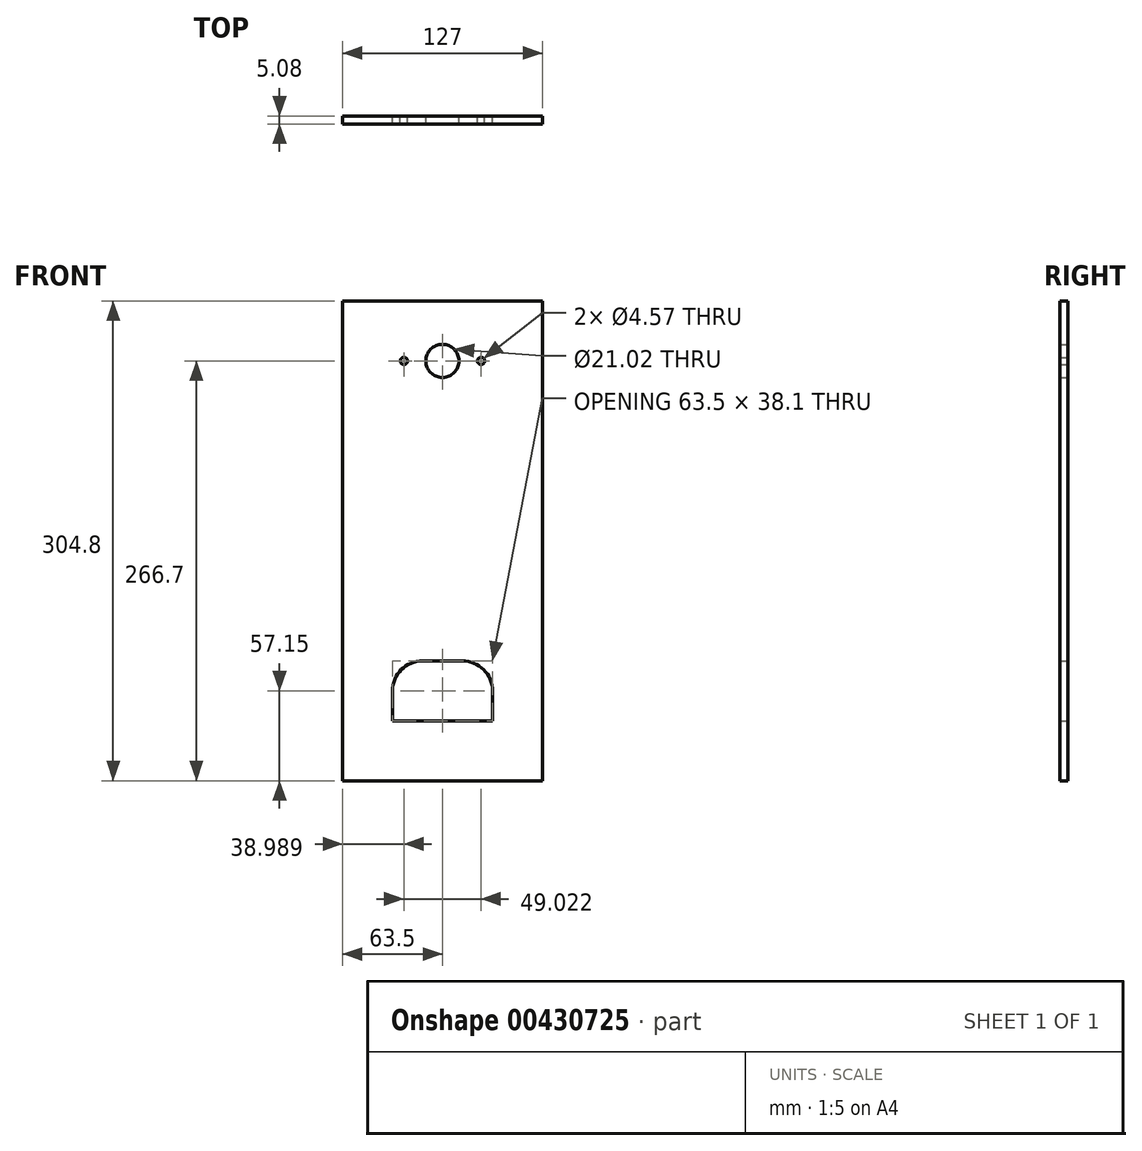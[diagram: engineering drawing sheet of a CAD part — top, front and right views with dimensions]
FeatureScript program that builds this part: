
annotation { "Feature Type Name" : "Feature", "Feature Type Description" : "" }
export const myFeature = defineFeature(function(context is Context, id is Id, definition is map)
    precondition{}
    {
        {
            var Q0;
            Q0=qCreatedBy(makeId("Front.planeOp"),FACE);
            var sketch = newSketch(context, id + "F0", { "sketchPlane" : qUnion([Q0])});
            skLineSegment(sketch, "E0.bottom", {"start": v(0, 0) * mm, "end": v(127, 0) * mm});
            skLineSegment(sketch, "E0.top", {"start": v(0, -304.8) * mm, "end": v(127, -304.8) * mm});
            skLineSegment(sketch, "E0.left", {"start": v(0, 0) * mm, "end": v(0, -304.8) * mm});
            skLineSegment(sketch, "E0.right", {"start": v(127, 0) * mm, "end": v(127, -304.8) * mm});
            skCircle(sketch, "E1", {"center": v(63.5, -38.1) * mm, "radius": 10.5 * mm});
            skLineSegment(sketch, "E2", {"start": v(63.5, 0) * mm, "end": v(63.5, -304.8) * mm, "construction": true});
            skCircle(sketch, "E3", {"center": v(88.01, -38.1) * mm, "radius": 2.29 * mm});
            skLineSegment(sketch, "E4", {"start": v(63.5, -38.1) * mm, "end": v(127, -38.1) * mm, "construction": true});
            skCircle(sketch, "E5.MirrorC", {"center": v(38.99, -38.1) * mm, "radius": 2.29 * mm});
            skLineSegment(sketch, "E6.bottom", {"start": v(31.75, -266.7) * mm, "end": v(95.25, -266.7) * mm});
            skLineSegment(sketch, "E6.top", {"start": v(50.8, -228.6) * mm, "end": v(76.2, -228.6) * mm});
            skLineSegment(sketch, "E6.left", {"start": v(31.75, -266.7) * mm, "end": v(31.75, -247.65) * mm});
            skLineSegment(sketch, "E6.right", {"start": v(95.25, -266.7) * mm, "end": v(95.25, -247.65) * mm});
            skPoint(sketch, "E7.visualSharp", {"position": v(31.75, -228.6) * mm});
            skArc(sketch, "E7.filletArc", {"start": v(50.8, -228.6) * mm, "mid": v(37.33, -234.18) * mm, "end": v(31.75, -247.65) * mm});
            skPoint(sketch, "E8.visualSharp", {"position": v(95.25, -228.6) * mm});
            skArc(sketch, "E8.filletArc", {"start": v(95.25, -247.65) * mm, "mid": v(89.67, -234.18) * mm, "end": v(76.2, -228.6) * mm});
            skSolve(sketch);
        }
        {
            var Q0;
            Q0 = qSketchRegion(id + "F0", true);
            extrude(context, id + "F1", {"entities" : qUnion([Q0]), "depth" : 5.08 * mm});
        }
    });
